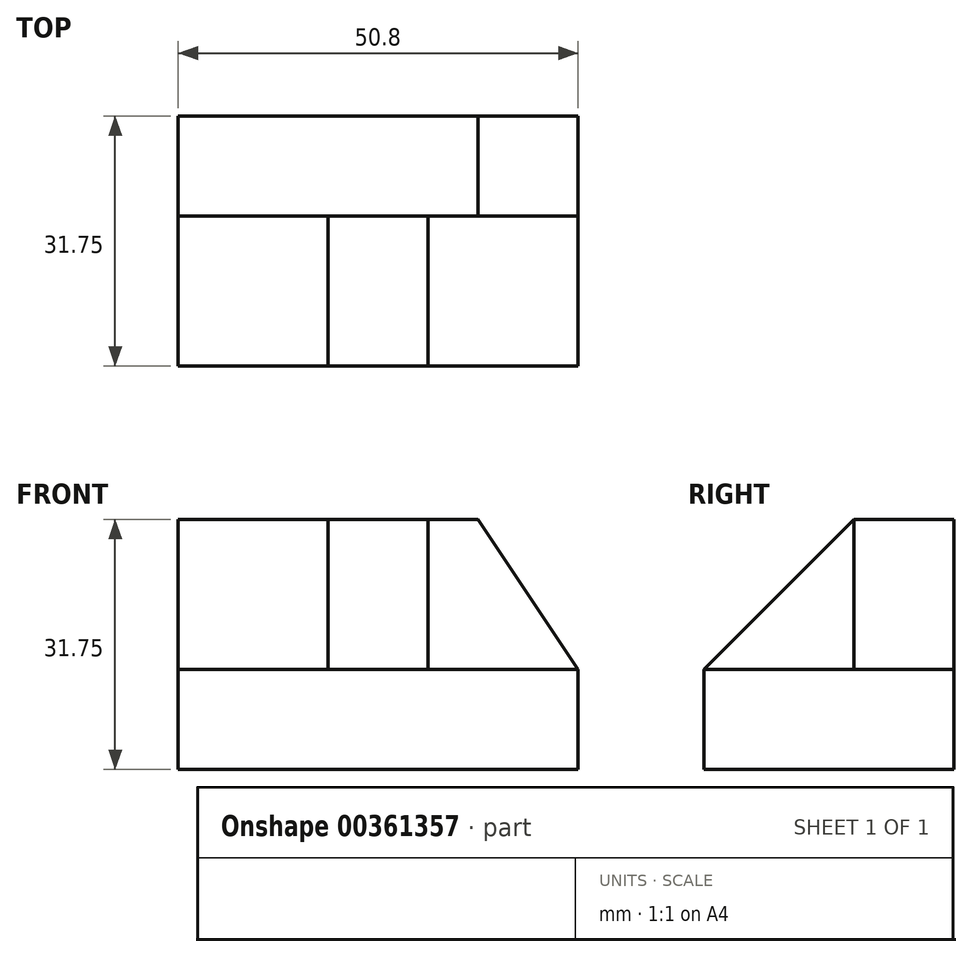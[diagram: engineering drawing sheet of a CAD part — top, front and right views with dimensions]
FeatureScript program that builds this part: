
annotation { "Feature Type Name" : "Feature", "Feature Type Description" : "" }
export const myFeature = defineFeature(function(context is Context, id is Id, definition is map)
    precondition{}
    {
        {
            var Q0;
            Q0=qCreatedBy(makeId("Front.planeOp"),FACE);
            var sketch = newSketch(context, id + "F0", { "sketchPlane" : qUnion([Q0])});
            skLineSegment(sketch, "E0", {"start": v(0, 0) * mm, "end": v(0, 31.75) * mm});
            skLineSegment(sketch, "E1", {"start": v(0, 31.75) * mm, "end": v(38.1, 31.75) * mm});
            skLineSegment(sketch, "E2", {"start": v(38.1, 31.75) * mm, "end": v(50.8, 12.7) * mm});
            skLineSegment(sketch, "E3", {"start": v(50.8, 12.7) * mm, "end": v(50.8, 0) * mm});
            skLineSegment(sketch, "E4", {"start": v(50.8, 0) * mm, "end": v(0, 0) * mm});
            skSolve(sketch);
        }
        {
            var Q0;
            Q0=makeQuery(id+"F0.imprint","IMPRINT",FACE,{"disambiguationData":[TD([[makeQuery(id+"F0.imprint","IMPRINT",EDGE,{"derivedFrom":sQuery(id+"F0.wireOp",EDGE,"E0")}),-1.0]])]});
            extrude(context, id + "F1", {"entities" : qUnion([Q0]), "depth" : 31.75 * mm});
        }
        {
            var Q0;
            Q0=makeQuery(id+"F1.opExtrude","CAP_FACE",FACE,{"disambiguationData":[OSD([sQuery(id+"F0.wireOp",EDGE,"E0"),sQuery(id+"F0.wireOp",EDGE,"E1"),sQuery(id+"F0.wireOp",EDGE,"E2"),sQuery(id+"F0.wireOp",EDGE,"E3"),sQuery(id+"F0.wireOp",EDGE,"E4")])],"isStart":false});
            var sketch = newSketch(context, id + "F2", { "sketchPlane" : qUnion([Q0])});
            skLineSegment(sketch, "E5", {"start": v(38.1, 31.75) * mm, "end": v(50.8, 12.7) * mm});
            skLineSegment(sketch, "E6", {"start": v(0, 12.7) * mm, "end": v(50.8, 12.7) * mm});
            skPoint(sketch, "E6.startSnap0", {"position": v(0, 15.88) * mm});
            skLineSegment(sketch, "E7", {"start": v(0, 12.7) * mm, "end": v(0, 31.75) * mm});
            skLineSegment(sketch, "E8", {"start": v(0, 31.75) * mm, "end": v(38.1, 31.75) * mm});
            skSolve(sketch);
        }
        {
            var Q0;
            Q0=makeQuery(id+"F2.imprint","IMPRINT",FACE,{"disambiguationData":[TD([[makeQuery(id+"F2.imprint","IMPRINT",EDGE,{"derivedFrom":sQuery(id+"F2.wireOp",EDGE,"E5")}),-1.0]])]});
            extrude(context, id + "F3", {"entities" : qUnion([Q0]), "operationType" : NewBodyOperationType.REMOVE, "oppositeDirection" : true, "depth" : 19.05 * mm});
        }
        {
            var Q0;
            Q0=makeQuery(id+"F3.boolean.opBoolean","COPY",FACE,{"derivedFrom":makeQuery(id+"F3.opExtrude","CAP_FACE",FACE,{"disambiguationData":[OSD([sQuery(id+"F2.wireOp",EDGE,"E5"),sQuery(id+"F2.wireOp",EDGE,"E6"),sQuery(id+"F2.wireOp",EDGE,"E7"),sQuery(id+"F2.wireOp",EDGE,"E8")])],"isStart":false})});
            var sketch = newSketch(context, id + "F4", { "sketchPlane" : qUnion([Q0])});
            skLineSegment(sketch, "E9", {"start": v(0, 31.75) * mm, "end": v(19.05, 31.75) * mm});
            skLineSegment(sketch, "E10", {"start": v(19.05, 31.75) * mm, "end": v(19.05, 12.7) * mm});
            skLineSegment(sketch, "E11", {"start": v(19.05, 12.7) * mm, "end": v(31.75, 12.7) * mm});
            skLineSegment(sketch, "E12", {"start": v(31.75, 12.7) * mm, "end": v(31.75, 31.75) * mm});
            skLineSegment(sketch, "E13", {"start": v(31.75, 31.75) * mm, "end": v(19.05, 31.75) * mm});
            skSolve(sketch);
        }
        {
            var Q0;
            Q0 = qSketchRegion(id + "F4", true);
            extrude(context, id + "F5", {"entities" : qUnion([Q0]), "operationType" : NewBodyOperationType.ADD, "depth" : 19.05 * mm});
        }
        {
            var Q0;
            Q0=makeQuery(id+"F5.opExtrude","SWEPT_FACE",FACE,{"disambiguationData":[OSD([sQuery(id+"F4.wireOp",EDGE,"E12")])]});
            var sketch = newSketch(context, id + "F6", { "sketchPlane" : qUnion([Q0])});
            skLineSegment(sketch, "E14", {"start": v(-12.7, 31.75) * mm, "end": v(-31.75, 12.7) * mm});
            skLineSegment(sketch, "E15", {"start": v(-31.75, 12.7) * mm, "end": v(-31.75, 31.75) * mm});
            skLineSegment(sketch, "E16", {"start": v(-31.75, 31.75) * mm, "end": v(-12.7, 31.75) * mm});
            skSolve(sketch);
        }
        {
            var Q0;
            Q0=makeQuery(id+"F6.imprint","IMPRINT",FACE,{"disambiguationData":[TD([[makeQuery(id+"F6.imprint","IMPRINT",EDGE,{"derivedFrom":sQuery(id+"F6.wireOp",EDGE,"E14")}),-1.0]])]});
            var Q1;
            Q1=makeQuery(id+"F6.imprint","IMPRINT",FACE,{"disambiguationData":[TD([[makeQuery(id+"F6.imprint","IMPRINT",EDGE,{"derivedFrom":sQuery(id+"F6.wireOp",EDGE,"E14")}),-1.0]])]});
            extrude(context, id + "F7", {"entities" : qUnion([Q0, Q1]), "operationType" : NewBodyOperationType.REMOVE, "oppositeDirection" : true, "depth" : 25.4 * mm});
        }
    });
